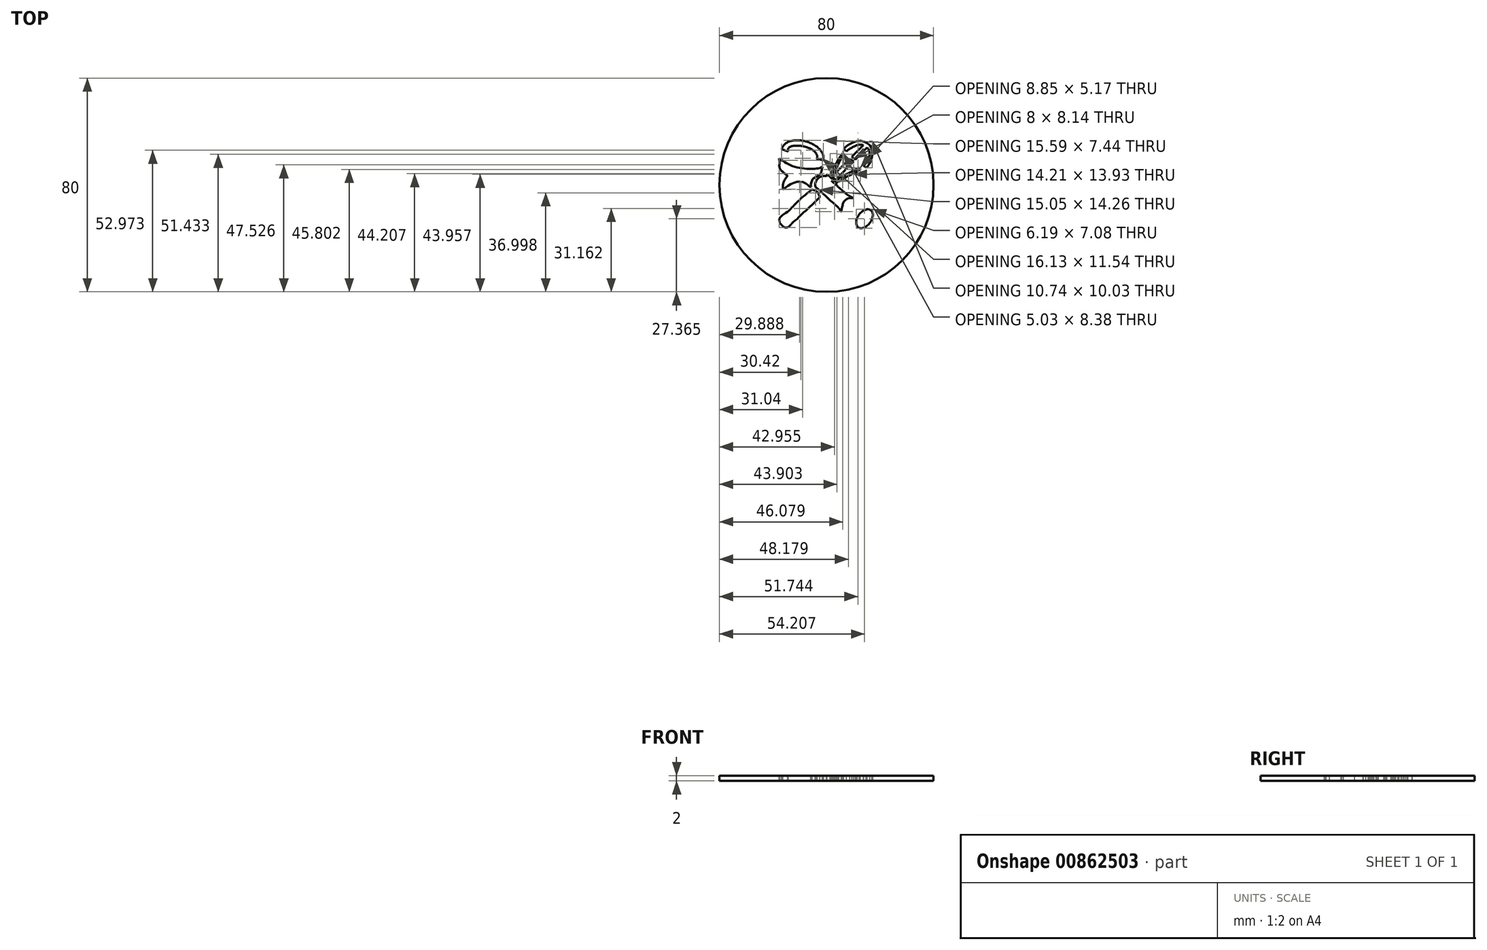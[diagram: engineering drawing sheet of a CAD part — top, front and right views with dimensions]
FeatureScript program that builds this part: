
annotation { "Feature Type Name" : "Feature", "Feature Type Description" : "" }
export const myFeature = defineFeature(function(context is Context, id is Id, definition is map)
    precondition{}
    {
        {
            var Q0;
            Q0=qCreatedBy(makeId("Top.planeOp"),FACE);
            var sketch = newSketch(context, id + "F0", { "sketchPlane" : qUnion([Q0])});
            skCircle(sketch, "E0", {"center": v(0, 0) * mm, "radius": 22.5 * mm});
            skSolve(sketch);
        }
        {
            var Q0;
            Q0=qCreatedBy(makeId("Top.planeOp"),FACE);
            var sketch = newSketch(context, id + "F1", { "sketchPlane" : qUnion([Q0])});
            skFitSpline(sketch, "E1", {"points": [v(1.22, 5.5) * mm, v(2.37, 7.32) * mm, v(3.65, 9.78) * mm, v(5.82, 12.86) * mm, v(8.5, 15.18) * mm, v(11.97, 16.53) * mm, v(14.73, 15.9) * mm, v(16.44, 14.47) * mm, v(17.07, 12.45) * mm, v(17.1, 10.73) * mm, v(16.2, 8.2) * mm, v(14.18, 5.87) * mm, v(10.4, 3.65) * mm, v(8.23, 2.78) * mm, v(5.86, 1.57) * mm, v(3.41, 0.24) * mm, v(3.35, 0.2) * mm, v(1.59, 1.72) * mm, v(0, 3.17) * mm, v(1.22, 5.5) * mm]});
            skLineSegment(sketch, "E2", {"start": v(0.2, 3.96) * mm, "end": v(3.96, 0.58) * mm});
            skPoint(sketch, "E3.orphan", {"position": v(4.61, 0) * mm});
            skFitSpline(sketch, "E4", {"points": [v(1.94, 3.9) * mm, v(3.28, 6.07) * mm, v(4.97, 9.45) * mm, v(7.15, 12.38) * mm, v(10.24, 14.37) * mm, v(12.61, 15.08) * mm, v(14.18, 14.8) * mm, v(14.3, 14.73) * mm], "startDerivative": vector(8.83, 13.39) * mm, "endDerivative": vector(2.33, -1.6) * mm});
            skLineSegment(sketch, "E5", {"start": v(14.3, 14.73) * mm, "end": v(10.07, 10.38) * mm});
            skLineSegment(sketch, "E6", {"start": v(5.62, 5.8) * mm, "end": v(2.92, 3.19) * mm});
            skLineSegment(sketch, "E7", {"start": v(2.92, 3.19) * mm, "end": v(1.94, 3.9) * mm});
            skLineSegment(sketch, "E8", {"start": v(14.95, 14.26) * mm, "end": v(10.68, 9.87) * mm});
            skFitSpline(sketch, "E9", {"points": [v(14.95, 14.26) * mm, v(15.92, 12.83) * mm, v(15.85, 10.11) * mm, v(13.91, 7.24) * mm, v(10.11, 4.87) * mm, v(8.05, 3.97) * mm, v(5.33, 2.46) * mm, v(4.56, 1.86) * mm], "startDerivative": vector(9.83, -10.61) * mm, "endDerivative": vector(-6.81, -6.05) * mm});
            skLineSegment(sketch, "E10", {"start": v(3.54, 2.55) * mm, "end": v(4.38, 1.73) * mm});
            skLineSegment(sketch, "E11", {"start": v(4.38, 1.73) * mm, "end": v(4.56, 1.86) * mm});
            skLineSegment(sketch, "E12", {"start": v(6.37, 13.46) * mm, "end": v(7.4, 12.6) * mm});
            skLineSegment(sketch, "E13", {"start": v(5.28, 12.2) * mm, "end": v(6.24, 11.42) * mm});
            skLineSegment(sketch, "E14.trimOffspring", {"start": v(8.95, 9.22) * mm, "end": v(5.62, 5.8) * mm});
            skLineSegment(sketch, "E15.trimOffspring", {"start": v(9.56, 8.72) * mm, "end": v(3.54, 2.55) * mm});
            skLineSegment(sketch, "E16.trimOffspring", {"start": v(10.07, 10.38) * mm, "end": v(10.68, 9.87) * mm});
            skLineSegment(sketch, "E17.trimOffspring", {"start": v(8.95, 9.22) * mm, "end": v(9.56, 8.72) * mm});
            skLineSegment(sketch, "E18.trimOffspring", {"start": v(13.87, 7.2) * mm, "end": v(14.83, 6.42) * mm});
            skLineSegment(sketch, "E19.trimOffspring", {"start": v(12.59, 6.25) * mm, "end": v(13.59, 5.43) * mm});
            skSolve(sketch);
        }
        {
            var Q0;
            Q0=makeQuery(id+"F0.imprint","IMPRINT",FACE,{"disambiguationData":[TD([[makeQuery(id+"F0.imprint","IMPRINT",EDGE,{"derivedFrom":sQuery(id+"F0.wireOp",EDGE,"E0")}),1.0]])]});
            var sketch = newSketch(context, id + "F2", { "sketchPlane" : qUnion([Q0])});
            skFitSpline(sketch, "E20", {"points": [v(-0.35, 3.38) * mm, v(6.83, -2.91) * mm, v(7.82, -3.68) * mm, v(8.5, -4.08) * mm, v(10.06, -4.94) * mm, v(12.36, -6.3) * mm, v(15.53, -8.4) * mm, v(16.97, -9.67) * mm, v(17.3, -11.24) * mm, v(17, -12.8) * mm, v(16.2, -14.21) * mm, v(15.25, -15.2) * mm, v(13.8, -16.03) * mm, v(12.36, -16.12) * mm, v(11.01, -15.32) * mm, v(8.74, -13.57) * mm, v(6.8, -11.6) * mm, v(5.08, -9.42) * mm, v(4.53, -8.62) * mm, v(4.13, -8.23) * mm, v(1.43, -5.8) * mm, v(-1.89, -2.7) * mm, v(-3.6, -1.16) * mm, v(-4.22, -0.58) * mm, v(-4.1, 0.96) * mm, v(-3.36, 2.25) * mm, v(-2.01, 3.17) * mm, v(-0.5, 3.4) * mm, v(-0.43, 3.4) * mm, v(-0.35, 3.38) * mm]});
            skFitSpline(sketch, "E21", {"points": [v(10.06, -4.94) * mm, v(8.27, -4.94) * mm, v(7.07, -5.64) * mm, v(6.45, -6.37) * mm, v(5.99, -7.61) * mm, v(5.56, -9.7) * mm, v(5.48, -9.97) * mm, v(5.48, -9.97) * mm], "startDerivative": vector(-9.38, 1.07) * mm, "endDerivative": vector(-0.2, 0.46) * mm});
            skFitSpline(sketch, "E22", {"points": [v(7.82, -3.68) * mm, v(6.82, -3.84) * mm, v(5.85, -4.46) * mm, v(5.21, -5.37) * mm, v(4.67, -6.93) * mm, v(4.35, -8.43) * mm], "startDerivative": vector(-5.65, -0.35) * mm, "endDerivative": vector(-1.3, -6.71) * mm});
            skFitSpline(sketch, "E23", {"points": [v(-5.33, -1.7) * mm, v(-3.72, -2.33) * mm, v(-2.99, -3.28) * mm, v(-2.51, -4.48) * mm, v(-2.8, -4.85) * mm, v(-4.38, -6.46) * mm, v(-6.6, -8.54) * mm, v(-9.42, -11.13) * mm, v(-10.95, -12.67) * mm, v(-12.74, -14.2) * mm, v(-13.7, -15.22) * mm, v(-14.57, -15.88) * mm, v(-15.4, -15.92) * mm, v(-16.32, -15.52) * mm, v(-16.98, -15.04) * mm, v(-17.42, -14.24) * mm, v(-17.64, -13.21) * mm, v(-17.45, -12.3) * mm, v(-16.87, -11.68) * mm, v(-16.32, -11.2) * mm, v(-14.42, -9.9) * mm, v(-12.96, -8.47) * mm, v(-10.99, -6.46) * mm, v(-9.24, -4.78) * mm, v(-7.63, -3.46) * mm, v(-5.8, -2) * mm, v(-5.45, -1.76) * mm], "startDerivative": vector(44.34, -12.44) * mm, "endDerivative": vector(13.73, 8.38) * mm});
            skFitSpline(sketch, "E24", {"points": [v(-5.45, -1.76) * mm, v(-5.44, -1.76) * mm, v(-5.33, -1.7) * mm], "startDerivative": vector(0.12, 0.08) * mm, "endDerivative": vector(0.12, 0.03) * mm});
            skFitSpline(sketch, "E25", {"points": [v(16.97, -9.67) * mm, v(15.53, -9.09) * mm, v(13.78, -9.67) * mm, v(12.5, -10.62) * mm, v(11.59, -11.99) * mm, v(11.2, -13.08) * mm, v(11.1, -13.96) * mm, v(11.2, -14.8) * mm, v(11.54, -15.7) * mm], "startDerivative": vector(-10.12, 6.24) * mm, "endDerivative": vector(3.75, -8.13) * mm});
            skFitSpline(sketch, "E26", {"points": [v(15.53, -8.4) * mm, v(14.5, -8.4) * mm, v(13.03, -8.8) * mm, v(11.85, -9.6) * mm, v(10.74, -11.07) * mm, v(10.27, -12.7) * mm, v(10.14, -14.67) * mm], "startDerivative": vector(-7.17, 0.43) * mm, "endDerivative": vector(-0.37, -10.77) * mm});
            skFitSpline(sketch, "E27", {"points": [v(-16.87, -11.68) * mm, v(-15.95, -11.84) * mm, v(-15.1, -12.36) * mm, v(-14.3, -13.38) * mm, v(-13.9, -14.6) * mm, v(-13.92, -15.45) * mm], "startDerivative": vector(5.23, -0.23) * mm, "endDerivative": vector(-0.55, -4.46) * mm});
            skFitSpline(sketch, "E28", {"points": [v(-15.77, -10.83) * mm, v(-14.39, -11.37) * mm, v(-13.45, -12.33) * mm, v(-13.02, -13.43) * mm, v(-12.9, -14.02) * mm, v(-12.9, -14.36) * mm], "startDerivative": vector(5.77, -1.75) * mm, "endDerivative": vector(0, -0.14) * mm});
            skFitSpline(sketch, "E29.trimOffspring", {"points": [v(-5.33, -1.7) * mm, v(-3.72, -2.33) * mm, v(-2.99, -3.28) * mm, v(-2.51, -4.48) * mm, v(-2.8, -4.85) * mm, v(-4.38, -6.46) * mm, v(-6.6, -8.54) * mm, v(-9.42, -11.13) * mm, v(-10.95, -12.67) * mm, v(-12.74, -14.2) * mm, v(-13.7, -15.22) * mm, v(-14.57, -15.88) * mm, v(-15.4, -15.92) * mm, v(-16.32, -15.52) * mm, v(-16.98, -15.04) * mm, v(-17.42, -14.24) * mm, v(-17.64, -13.21) * mm, v(-17.45, -12.3) * mm, v(-16.87, -11.68) * mm, v(-16.32, -11.2) * mm, v(-14.42, -9.9) * mm, v(-12.96, -8.47) * mm, v(-10.99, -6.46) * mm, v(-9.24, -4.78) * mm, v(-7.63, -3.46) * mm, v(-5.8, -2) * mm, v(-5.45, -1.76) * mm], "startDerivative": vector(44.34, -12.44) * mm, "endDerivative": vector(13.73, 8.38) * mm});
            skSolve(sketch);
        }
        {
            var Q0;
            Q0=makeQuery(id+"F0.imprint","IMPRINT",FACE,{"disambiguationData":[TD([[makeQuery(id+"F0.imprint","IMPRINT",EDGE,{"derivedFrom":sQuery(id+"F0.wireOp",EDGE,"E0")}),1.0]])]});
            var sketch = newSketch(context, id + "F3", { "sketchPlane" : qUnion([Q0])});
            skFitSpline(sketch, "E30", {"points": [v(-5.3, 2.03) * mm, v(-5.46, 1.34) * mm, v(-5.66, 0.8) * mm, v(-5.84, 0.29) * mm, v(-5.84, -0.17) * mm, v(-5.76, -0.5) * mm, v(-5.82, -0.65) * mm, v(-5.93, -0.74) * mm, v(-6.18, -0.7) * mm, v(-6.64, -0.39) * mm, v(-7.4, 0.32) * mm, v(-8.47, 0.92) * mm, v(-10.02, 1.23) * mm, v(-11.65, 1.04) * mm, v(-13.6, 0.2) * mm, v(-15.02, -0.81) * mm, v(-15.65, -1.4) * mm, v(-15.96, -1.63) * mm, v(-16.13, -1.61) * mm, v(-16.24, -1.55) * mm, v(-16.34, -0.64) * mm, v(-16.1, 0.79) * mm, v(-15.44, 2.26) * mm, v(-14.73, 3.27) * mm, v(-14.58, 3.52) * mm, v(-14.6, 3.53) * mm, v(-14.87, 3.69) * mm, v(-16.52, 5.03) * mm, v(-17.55, 6.5) * mm, v(-17.61, 8.31) * mm, v(-17.57, 10.89) * mm, v(-16.8, 13.22) * mm, v(-16.23, 14.55) * mm, v(-14.54, 15.99) * mm, v(-12.52, 16.63) * mm, v(-9.24, 16.6) * mm, v(-6.48, 15.89) * mm, v(-3.21, 13.97) * mm, v(-1.82, 12.36) * mm, v(-1.4, 11.61) * mm, v(-1.17, 10.4) * mm, v(-1.39, 7.46) * mm, v(-1.82, 5.36) * mm, v(-2.5, 3.99) * mm, v(-5.3, 2.03) * mm]});
            skFitSpline(sketch, "E31", {"points": [v(-1.82, 5.36) * mm, v(-4.7, 3.83) * mm, v(-7.9, 3.77) * mm, v(-11.24, 4.32) * mm, v(-14.58, 5.36) * mm, v(-17.01, 7.14) * mm, v(-17.61, 8.31) * mm], "startDerivative": vector(-9.26, -19.05) * mm, "endDerivative": vector(-5.93, 9.27) * mm});
            skFitSpline(sketch, "E32", {"points": [v(-14.58, 3.52) * mm, v(-12.39, 2.62) * mm, v(-10.74, 2.48) * mm, v(-7.52, 2.24) * mm, v(-5.3, 2.03) * mm], "startDerivative": vector(9.2, -4.42) * mm, "endDerivative": vector(8.38, -0.78) * mm});
            skFitSpline(sketch, "E33", {"points": [v(-9, 14.52) * mm, v(-5.98, 13.54) * mm, v(-4.04, 12) * mm, v(-3.44, 10.56) * mm, v(-4.04, 9.4) * mm, v(-6.34, 8.83) * mm, v(-10.09, 9.52) * mm, v(-13.02, 10.89) * mm, v(-14.41, 12.83) * mm, v(-13.95, 14.06) * mm, v(-12.06, 14.66) * mm, v(-10.28, 14.66) * mm, v(-9, 14.52) * mm]});
            skFitSpline(sketch, "E34", {"points": [v(-17.64, 9.98) * mm, v(-13.06, 7.21) * mm, v(-6.58, 6.02) * mm, v(-3.08, 6.25) * mm, v(-1.51, 6.76) * mm], "startDerivative": vector(14.48, -10.8) * mm, "endDerivative": vector(8.92, 3.6) * mm});
            skFitSpline(sketch, "E35", {"points": [v(-17.61, 8.31) * mm, v(-15.02, 6.68) * mm, v(-11.88, 5.48) * mm, v(-8.1, 4.9) * mm, v(-4.15, 4.75) * mm, v(-1.82, 5.36) * mm], "startDerivative": vector(13, -8.92) * mm, "endDerivative": vector(12.57, 4.52) * mm});
            skLineSegment(sketch, "E36", {"start": v(-8.52, 14.42) * mm, "end": v(-8.05, 16.4) * mm});
            skLineSegment(sketch, "E37", {"start": v(-6.94, 16.07) * mm, "end": v(-7.4, 14.11) * mm});
            skLineSegment(sketch, "E38", {"start": v(-14.07, 13.94) * mm, "end": v(-16.13, 14.68) * mm});
            skLineSegment(sketch, "E39", {"start": v(-16.76, 13.33) * mm, "end": v(-14.33, 12.52) * mm});
            skLineSegment(sketch, "E40", {"start": v(-3.67, 9.8) * mm, "end": v(-1.19, 9.25) * mm});
            skLineSegment(sketch, "E41", {"start": v(-1.17, 10.37) * mm, "end": v(-3.49, 10.95) * mm});
            skPoint(sketch, "E42.start.orphan", {"position": v(-7.52, 13.64) * mm});
            skPoint(sketch, "E43.end.orphan", {"position": v(-17.66, 13.64) * mm});
            skSolve(sketch);
        }
        {
            var Q0;
            Q0=qCreatedBy(makeId("Top.planeOp"),FACE);
            var sketch = newSketch(context, id + "F4", { "sketchPlane" : qUnion([Q0])});
            skCircle(sketch, "E44", {"center": v(0, 0) * mm, "radius": 40 * mm});
            skSolve(sketch);
        }
        {
            var Q0;
            Q0=makeQuery(id+"F4.imprint","IMPRINT",FACE,{"disambiguationData":[TD([[makeQuery(id+"F4.imprint","IMPRINT",EDGE,{"derivedFrom":sQuery(id+"F4.wireOp",EDGE,"E44")}),1.0]])]});
            extrude(context, id + "F5", {"entities" : qUnion([Q0]), "oppositeDirection" : true, "depth" : 2 * mm, "offsetDistance" : 25 * mm});
        }
        {
            var Q0;
            Q0=makeQuery(id+"F2.imprint","IMPRINT",FACE,{"disambiguationData":[TD([[makeQuery(id+"F2.imprint","IMPRINT",EDGE,{"derivedFrom":sQuery(id+"F2.wireOp",EDGE,"E25")}),1.0]])]});
            var Q1;
            Q1=makeQuery(id+"F2.imprint","IMPRINT",FACE,{"disambiguationData":[TD([[makeQuery(id+"F2.imprint","IMPRINT",EDGE,{"derivedFrom":sQuery(id+"F2.wireOp",EDGE,"E20")}),-1.0]])]});
            var Q2;
            Q2=makeQuery(id+"F2.imprint","IMPRINT",FACE,{"disambiguationData":[TD([[makeQuery(id+"F2.imprint","IMPRINT",EDGE,{"derivedFrom":sQuery(id+"F2.wireOp",EDGE,"E22")}),-1.0]])]});
            var Q3;
            Q3=makeQuery(id+"F2.imprint","IMPRINT",FACE,{"disambiguationData":[TD([[makeQuery(id+"F2.imprint","IMPRINT",EDGE,{"derivedFrom":sQuery(id+"F2.wireOp",EDGE,"E23")}),-1.0]])]});
            var Q4;
            {var subQ0=sQuery(id+"F2.wireOp",EDGE,"E27");Q4=makeQuery(id+"F2.imprint","IMPRINT",FACE,{"disambiguationData":[TD([[makeQuery(id+"F2.imprint","IMPRINT",EDGE,{"derivedFrom":subQ0}),-1.0]])]});}
            var Q5;
            Q5=makeQuery(id+"F3.imprint","IMPRINT",FACE,{"disambiguationData":[TD([[makeQuery(id+"F3.imprint","IMPRINT",EDGE,{"derivedFrom":sQuery(id+"F3.wireOp",EDGE,"E30")}),-1.0]])]});
            var Q6;
            Q6=makeQuery(id+"F3.imprint","IMPRINT",FACE,{"disambiguationData":[TD([[makeQuery(id+"F3.imprint","IMPRINT",EDGE,{"derivedFrom":sQuery(id+"F3.wireOp",EDGE,"E32")}),-1.0]])]});
            extrude(context, id + "F6", {"entities" : qUnion([Q0, Q1, Q2, Q3, Q4, Q5, Q6]), "operationType" : NewBodyOperationType.REMOVE, "endBound" : BoundingType.THROUGH_ALL, "oppositeDirection" : true, "depth" : 25 * mm, "offsetDistance" : 25 * mm});
        }
        {
            var Q0;
            Q0=makeQuery(id+"F1.imprint","IMPRINT",FACE,{"disambiguationData":[TD([[makeQuery(id+"F1.imprint","IMPRINT",EDGE,{"derivedFrom":sQuery(id+"F1.wireOp",EDGE,"E1")}),-1.0]])]});
            extrude(context, id + "F7", {"entities" : qUnion([Q0]), "operationType" : NewBodyOperationType.REMOVE, "endBound" : BoundingType.THROUGH_ALL, "oppositeDirection" : true, "depth" : 25 * mm, "offsetDistance" : 25 * mm});
        }
        {
            var Q0;
            Q0=makeQuery(id+"F3.imprint","IMPRINT",FACE,{"disambiguationData":[TD([[makeQuery(id+"F3.imprint","IMPRINT",EDGE,{"derivedFrom":sQuery(id+"F3.wireOp",EDGE,"E31")}),-1.0]])]});
            extrude(context, id + "F8", {"entities" : qUnion([Q0]), "operationType" : NewBodyOperationType.REMOVE, "endBound" : BoundingType.THROUGH_ALL, "oppositeDirection" : true, "depth" : 25 * mm, "offsetDistance" : 25 * mm});
        }
        {
            var Q0;
            Q0=makeQuery(id+"F1.imprint","IMPRINT",FACE,{"disambiguationData":[TD([[makeQuery(id+"F1.imprint","IMPRINT",EDGE,{"derivedFrom":sQuery(id+"F1.wireOp",EDGE,"E5")}),1.0]])]});
            extrude(context, id + "F9", {"entities" : qUnion([Q0]), "operationType" : NewBodyOperationType.REMOVE, "endBound" : BoundingType.THROUGH_ALL, "oppositeDirection" : true, "depth" : 25 * mm, "offsetDistance" : 25 * mm});
        }
        {
            var Q0;
            Q0=makeQuery(id+"F3.imprint","IMPRINT",FACE,{"disambiguationData":[TD([[makeQuery(id+"F3.imprint","IMPRINT",EDGE,{"derivedFrom":sQuery(id+"F3.wireOp",EDGE,"E36")}),1.0]])]});
            var Q1;
            Q1=makeQuery(id+"F3.imprint","IMPRINT",FACE,{"disambiguationData":[TD([[makeQuery(id+"F3.imprint","IMPRINT",EDGE,{"derivedFrom":sQuery(id+"F3.wireOp",EDGE,"E33")}),1.0]])]});
            extrude(context, id + "F10", {"entities" : qUnion([Q0, Q1]), "operationType" : NewBodyOperationType.REMOVE, "endBound" : BoundingType.THROUGH_ALL, "oppositeDirection" : true, "depth" : 25 * mm, "offsetDistance" : 25 * mm});
        }
        {
            var Q0;
            Q0=makeQuery(id+"F5.opExtrude","CAP_FACE",FACE,{"disambiguationData":[OSD([sQuery(id+"F4.wireOp",EDGE,"E44")])],"isStart":true});
            var sketch = newSketch(context, id + "F11", { "sketchPlane" : qUnion([Q0])});
            skLineSegment(sketch, "E45", {"start": v(3.79, 2.3) * mm, "end": v(10.08, 8.76) * mm});
            skLineSegment(sketch, "E46", {"start": v(15.55, 14.37) * mm, "end": v(14.38, 15.51) * mm});
            skLineSegment(sketch, "E47", {"start": v(14.38, 15.51) * mm, "end": v(9.42, 10.55) * mm});
            skPoint(sketch, "E47.endSnap0", {"position": v(2.08, 2.27) * mm});
            skLineSegment(sketch, "E48", {"start": v(2.08, 3.19) * mm, "end": v(3.54, 1.73) * mm});
            skLineSegment(sketch, "E49", {"start": v(3.79, 2.3) * mm, "end": v(3.54, 1.73) * mm});
            skLineSegment(sketch, "E50", {"start": v(10.08, 8.76) * mm, "end": v(8.75, 9.87) * mm});
            skLineSegment(sketch, "E51", {"start": v(10.7, 9.4) * mm, "end": v(9.42, 10.55) * mm});
            skLineSegment(sketch, "E52.trimOffspring", {"start": v(8.75, 9.87) * mm, "end": v(2.08, 3.19) * mm});
            skLineSegment(sketch, "E53.trimOffspring", {"start": v(10.7, 9.4) * mm, "end": v(15.55, 14.37) * mm});
            skSolve(sketch);
        }
        {
            var Q0;
            Q0 = qSketchRegion(id + "F11", true);
            extrude(context, id + "F12", {"entities" : qUnion([Q0]), "operationType" : NewBodyOperationType.REMOVE, "endBound" : BoundingType.THROUGH_ALL, "oppositeDirection" : true, "depth" : 25 * mm, "offsetDistance" : 25 * mm});
        }
        {
            var Q0;
            Q0=makeQuery(id+"F3.imprint","IMPRINT",FACE,{"disambiguationData":[TD([[makeQuery(id+"F3.imprint","IMPRINT",EDGE,{"derivedFrom":sQuery(id+"F3.wireOp",EDGE,"E30")}),1.0]])]});
            var sketch = newSketch(context, id + "F13", { "sketchPlane" : qUnion([Q0])});
            skFitSpline(sketch, "E54", {"points": [v(2.2, 3.73) * mm, v(3.32, 5.52) * mm, v(4.27, 7.5) * mm, v(5, 9) * mm, v(5.65, 10.13) * mm, v(6.55, 11.45) * mm, v(7.57, 12.51) * mm, v(9.13, 13.53) * mm, v(10.67, 14.22) * mm, v(11.66, 14.61) * mm, v(13.26, 14.7) * mm, v(14.12, 14.57) * mm, v(15, 13.82) * mm, v(15.6, 12.87) * mm, v(15.79, 11.56) * mm, v(15.55, 10.25) * mm, v(14.84, 8.79) * mm, v(13.45, 7.4) * mm, v(12.07, 6.41) * mm, v(9.3, 4.95) * mm, v(7.93, 4.29) * mm, v(6.68, 3.67) * mm, v(5.57, 3.02) * mm, v(4.6, 2.36) * mm, v(4.11, 1.98) * mm, v(3, 3.04) * mm, v(2.26, 3.58) * mm, v(2.17, 3.65) * mm, v(2.17, 3.68) * mm, v(2.18, 3.69) * mm, v(2.2, 3.73) * mm]});
            skLineSegment(sketch, "E55", {"start": v(2.2, 3.73) * mm, "end": v(1.68, 3.34) * mm});
            skLineSegment(sketch, "E56", {"start": v(1.68, 3.34) * mm, "end": v(1.39, 3.73) * mm});
            skLineSegment(sketch, "E57", {"start": v(1.39, 3.73) * mm, "end": v(4.7, 10) * mm});
            skLineSegment(sketch, "E58", {"start": v(4.7, 10) * mm, "end": v(5.88, 11.72) * mm});
            skLineSegment(sketch, "E59", {"start": v(5.88, 11.72) * mm, "end": v(6.42, 11.27) * mm});
            skLineSegment(sketch, "E60", {"start": v(7.57, 12.51) * mm, "end": v(7.38, 12.65) * mm});
            skFitSpline(sketch, "E61", {"points": [v(7.38, 12.65) * mm, v(7.38, 13.32) * mm, v(9.3, 14.51) * mm, v(12, 15.46) * mm, v(14.17, 15.55) * mm, v(15.03, 15.06) * mm, v(15.75, 13.93) * mm, v(16.33, 12.65) * mm, v(16.54, 10.93) * mm, v(16.15, 9.17) * mm, v(15.05, 7.62) * mm, v(14.21, 6.96) * mm, v(14.15, 7.03) * mm, v(13.87, 7.2) * mm, v(13.45, 7.62) * mm], "startDerivative": vector(-3.58, 12.7) * mm, "endDerivative": vector(-8.3, 9.46) * mm});
            skFitSpline(sketch, "E62", {"points": [v(4.11, 1.98) * mm, v(3.7, 1.49) * mm, v(4.26, 1.24) * mm, v(6.95, 2.72) * mm, v(9.98, 4.24) * mm, v(12.54, 5.94) * mm, v(12.59, 6.25) * mm, v(12.57, 6.26) * mm, v(12.15, 6.68) * mm], "startDerivative": vector(-6.87, -5.34) * mm, "endDerivative": vector(-6.12, 6.43) * mm});
            skSolve(sketch);
        }
        {
            var Q0;
            {var subQ0=sQuery(id+"F13.wireOp",EDGE,"E55");Q0=makeQuery(id+"F13.imprint","IMPRINT",FACE,{"disambiguationData":[TD([[makeQuery(id+"F13.imprint","IMPRINT",EDGE,{"derivedFrom":subQ0}),-1.0]])]});}
            var Q1;
            {var subQ0=sQuery(id+"F13.wireOp",EDGE,"E62");Q1=makeQuery(id+"F13.imprint","IMPRINT",FACE,{"disambiguationData":[TD([[makeQuery(id+"F13.imprint","IMPRINT",EDGE,{"derivedFrom":subQ0}),1.0]])]});}
            extrude(context, id + "F14", {"entities" : qUnion([Q0, Q1]), "operationType" : NewBodyOperationType.REMOVE, "endBound" : BoundingType.THROUGH_ALL, "oppositeDirection" : true, "depth" : 25 * mm, "offsetDistance" : 25 * mm});
        }
    });
